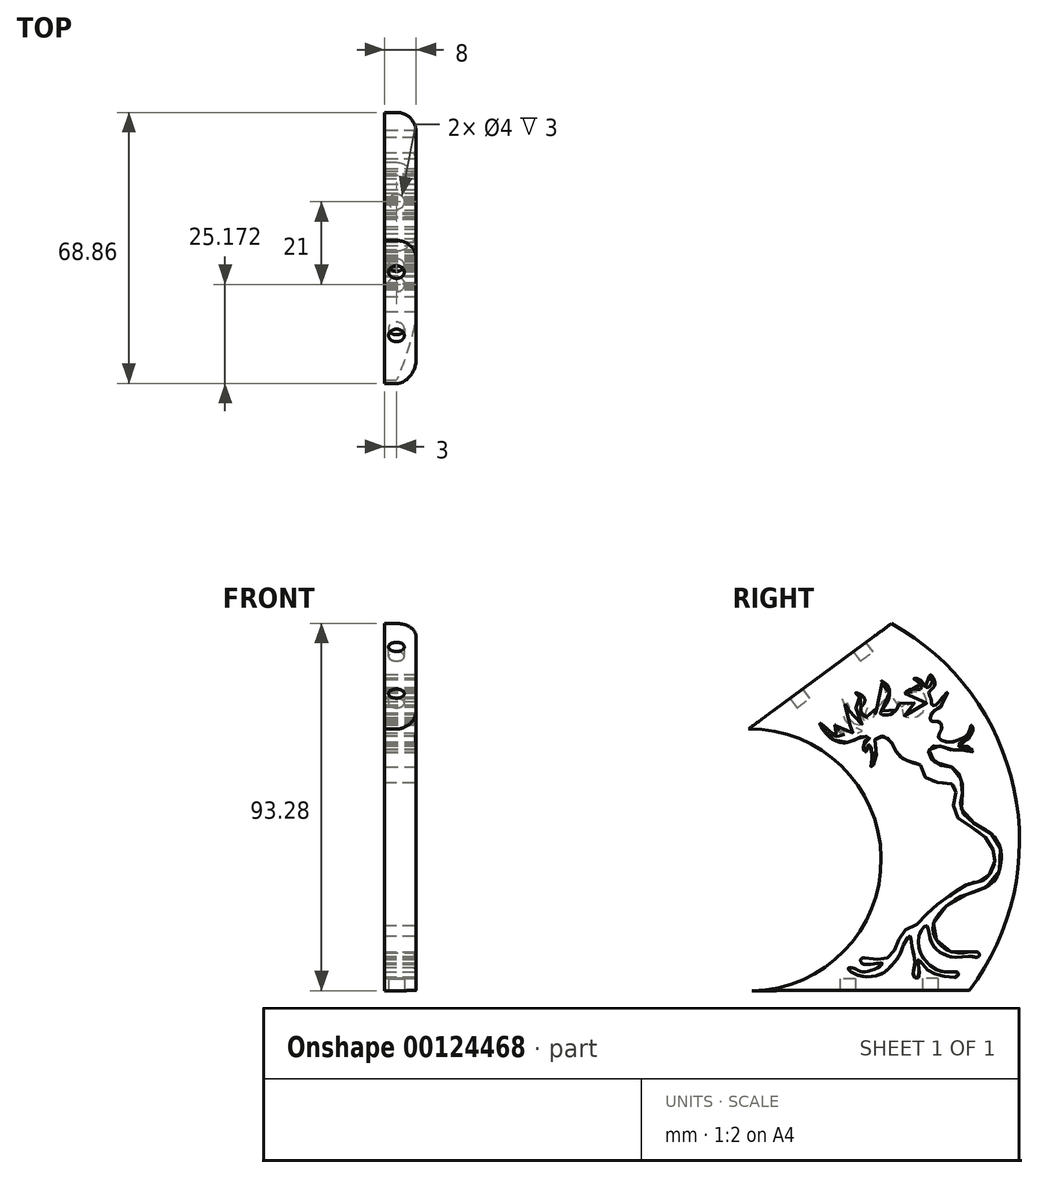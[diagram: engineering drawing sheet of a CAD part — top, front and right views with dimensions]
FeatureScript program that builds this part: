
annotation { "Feature Type Name" : "Feature", "Feature Type Description" : "" }
export const myFeature = defineFeature(function(context is Context, id is Id, definition is map)
    precondition{}
    {
        {
            var Q0;
            Q0=qCreatedBy(makeId("Right.planeOp"),FACE);
            var sketch = newSketch(context, id + "F0", { "sketchPlane" : qUnion([Q0])});
            skLineSegment(sketch, "E0", {"start": v(-38.95, 23.05) * mm, "end": v(-2.61, 49.85) * mm});
            skArc(sketch, "E1", {"start": v(-38.02, -43.43) * mm, "mid": v(-5.25, -9.73) * mm, "end": v(-38.95, 23.05) * mm});
            skArc(sketch, "E2", {"start": v(17.23, -43.32) * mm, "mid": v(28.53, 7.78) * mm, "end": v(-2.61, 49.85) * mm});
            skLineSegment(sketch, "E3", {"start": v(-38.02, -43.43) * mm, "end": v(17.23, -43.32) * mm});
            skArc(sketch, "E4.0", {"start": v(14.53, -41.3) * mm, "mid": v(25.24, 7.08) * mm, "end": v(-4.24, 46.9) * mm});
            skLineSegment(sketch, "E5", {"start": v(-4.24, 46.9) * mm, "end": v(-5.6, 47.65) * mm});
            skLineSegment(sketch, "E6", {"start": v(14.53, -41.3) * mm, "end": v(13, -43.33) * mm});
            skSolve(sketch);
        }
        {
            var Q0;
            Q0 = qSketchRegion(id + "F0", true);
            extrude(context, id + "F1", {"entities" : qUnion([Q0]), "oppositeDirection" : true, "depth" : 8 * mm});
        }
        {
            var Q0;
            Q0=makeQuery(id+"F1.opExtrude","CAP_FACE",FACE,{"disambiguationData":[OSD([sQuery(id+"F0.wireOp",EDGE,"E0"),sQuery(id+"F0.wireOp",EDGE,"E1"),sQuery(id+"F0.wireOp",EDGE,"E2"),sQuery(id+"F0.wireOp",EDGE,"E3")])],"isStart":true});
            var sketch = newSketch(context, id + "F2", { "sketchPlane" : qUnion([Q0])});
            skFitSpline(sketch, "E7", {"points": [v(4.67, 13.86) * mm, v(2.9, 14.45) * mm, v(-0.7, 16.28) * mm, v(-2.11, 18.67) * mm, v(-4.38, 21.18) * mm, v(-6.92, 20.26) * mm, v(-6.41, 17) * mm, v(-7.75, 13.26) * mm, v(-7.49, 17.25) * mm, v(-8.46, 19) * mm, v(-9.33, 17) * mm, v(-9.62, 19.7) * mm, v(-8.15, 20.8) * mm, v(-9.58, 21.26) * mm, v(-11.98, 20.2) * mm, v(-17.32, 20.28) * mm, v(-20.8, 24.44) * mm, v(-18.65, 22.73) * mm, v(-16.35, 21.16) * mm, v(-14.5, 21.7) * mm, v(-16.52, 22.58) * mm, v(-16.92, 24.07) * mm, v(-16.03, 22.88) * mm, v(-13.74, 22.44) * mm, v(-11.8, 21.99) * mm, v(-10.04, 22.46) * mm, v(-12.13, 23.55) * mm, v(-13.94, 24.64) * mm, v(-14.69, 26.12) * mm, v(-14.18, 28.48) * mm, v(-15.16, 30.73) * mm, v(-13.7, 29.56) * mm, v(-13.46, 28.36) * mm, v(-13.7, 26.36) * mm, v(-12.16, 24.47) * mm, v(-10.09, 24.24) * mm, v(-9.48, 25.75) * mm, v(-11.58, 26.98) * mm, v(-11.62, 28.54) * mm, v(-10.53, 30.64) * mm, v(-11.7, 32.24) * mm, v(-9.62, 31.09) * mm, v(-9.92, 29.08) * mm, v(-10.68, 28.21) * mm, v(-10.23, 27.01) * mm, v(-8.7, 28.47) * mm, v(-9.23, 27.1) * mm, v(-9.14, 26.26) * mm, v(-8.4, 25.5) * mm, v(-7.42, 25.87) * mm, v(-6.4, 27.9) * mm, v(-6.27, 28.46) * mm, v(-4.33, 30.58) * mm, v(-4.63, 33.99) * mm, v(-5.67, 35.46) * mm, v(-3.86, 34.43) * mm, v(-3.17, 32.53) * mm, v(-3.34, 30.6) * mm, v(-4.01, 29.23) * mm, v(-4.9, 28) * mm, v(-5.45, 26.99) * mm, v(-4.23, 26.6) * mm, v(-2.25, 27.14) * mm, v(-1.02, 29.1) * mm, v(-2.2, 31.06) * mm, v(-0.9, 30.16) * mm, v(-0.15, 28.69) * mm, v(1.46, 29.72) * mm, v(3.38, 29.77) * mm, v(1.97, 29.24) * mm, v(0.63, 28.56) * mm, v(0.17, 27.2) * mm, v(1.4, 25.95) * mm, v(4.8, 26.82) * mm, v(6.28, 30.56) * mm, v(4.23, 32.57) * mm, v(0.83, 32.13) * mm, v(2.44, 33.17) * mm, v(4.72, 33.08) * mm, v(4.61, 34.5) * mm, v(3.01, 35.89) * mm, v(4.88, 35.36) * mm, v(6.35, 33.55) * mm, v(7.46, 34.43) * mm, v(7.65, 35.36) * mm, v(7, 36.2) * mm, v(7.33, 36.78) * mm, v(8.14, 35.73) * mm, v(8.4, 34.24) * mm, v(7.5, 33.08) * mm, v(6.88, 32.14) * mm, v(7.42, 30.59) * mm, v(7.67, 29.17) * mm, v(8.6, 29.2) * mm, v(10.12, 30.8) * mm, v(11.58, 32.33) * mm, v(11.18, 31.18) * mm, v(10.43, 29.8) * mm, v(9.89, 28.72) * mm, v(8.76, 28.06) * mm, v(7.37, 26.6) * mm, v(7.49, 25.03) * mm, v(9.41, 24.94) * mm, v(10.1, 22.96) * mm, v(9.3, 20.95) * mm, v(11.68, 19.72) * mm, v(14.23, 20.22) * mm, v(16.96, 22) * mm, v(17.62, 24) * mm, v(18.07, 23.09) * mm, v(17.61, 21.58) * mm, v(16.16, 19.9) * mm, v(13.9, 19.07) * mm, v(14.9, 18.6) * mm, v(17.26, 18.51) * mm, v(18, 17.18) * mm, v(16.8, 17.43) * mm, v(15.07, 17.89) * mm, v(13, 17.7) * mm, v(10.79, 18.35) * mm, v(8.28, 18.86) * mm, v(6.95, 17.76) * mm, v(7.07, 15.98) * mm, v(10.33, 13.7) * mm, v(13.55, 13) * mm, v(15.13, 9.97) * mm, v(15.55, 7.42) * mm, v(14.9, 4.48) * mm, v(16.14, 0.88) * mm, v(20.85, -2.35) * mm, v(23.88, -4.74) * mm, v(25.24, -8.78) * mm, v(23.66, -15.24) * mm, v(19.31, -17.98) * mm, v(13.6, -20.26) * mm, v(8.6, -25.16) * mm, v(7.98, -28.8) * mm, v(10.27, -32.24) * mm, v(14.87, -33.9) * mm, v(19.5, -33.79) * mm, v(19.45, -34.86) * mm, v(17.8, -34.76) * mm, v(13.68, -34.93) * mm, v(11.25, -34.42) * mm, v(7.61, -31.45) * mm, v(6.3, -26.93) * mm, v(4.97, -28.03) * mm, v(4.2, -31.46) * mm, v(5.57, -35.28) * mm, v(10.47, -38.65) * mm, v(14.23, -38.82) * mm, v(13.96, -39.9) * mm, v(9.82, -39.5) * mm, v(6.57, -38.24) * mm, v(4.15, -35.38) * mm, v(4.36, -37.87) * mm, v(3.99, -40.3) * mm, v(2.9, -39.62) * mm, v(3.2, -37.47) * mm, v(3.06, -34.56) * mm, v(2.4, -31.01) * mm, v(2.01, -29.53) * mm, v(0.5, -31.63) * mm, v(-0.5, -34.36) * mm, v(-2.78, -37.26) * mm, v(-5.5, -39.4) * mm, v(-9.56, -39.88) * mm, v(-12.4, -38.97) * mm, v(-13.6, -37.74) * mm, v(-12.23, -37.74) * mm, v(-9.22, -38.68) * mm, v(-4.93, -36.6) * mm, v(-6.22, -36.5) * mm, v(-10.06, -36.52) * mm, v(-10.3, -35.32) * mm, v(-7.53, -35.25) * mm, v(-4.4, -35.38) * mm, v(-2.5, -34.12) * mm, v(-1.07, -31.45) * mm, v(0.35, -28.43) * mm, v(3.65, -26.78) * mm, v(7.2, -23.06) * mm, v(11.04, -20.18) * mm, v(17.2, -16.26) * mm, v(21.1, -15.1) * mm, v(23.56, -10.86) * mm, v(23.16, -7.74) * mm, v(20.23, -3.5) * mm, v(14.52, 0.2) * mm, v(13.13, 4.37) * mm, v(13.82, 7.94) * mm, v(11.44, 9.45) * mm, v(6.65, 9.97) * mm, v(4.67, 13.86) * mm]});
            skSolve(sketch);
        }
        {
            var Q0;
            Q0=makeQuery(id+"F1.opExtrude","CAP_EDGE",EDGE,{"disambiguationData":[OSD([sQuery(id+"F0.wireOp",EDGE,"E1")])],"isStart":true});
            var Q1;
            Q1=makeQuery(id+"F1.opExtrude","CAP_EDGE",EDGE,{"disambiguationData":[OSD([sQuery(id+"F0.wireOp",EDGE,"E2")])],"isStart":true});
            fillet(context, id + "F3", {"entities" : qUnion([Q0, Q1]), "radius" : 5 * mm, "tangentPropagation" : true, "allowEdgeOverflow" : false});
        }
        {
            var Q0;
            Q0 = qSketchRegion(id + "F2", true);
            extrude(context, id + "F4", {"entities" : qUnion([Q0]), "operationType" : NewBodyOperationType.REMOVE, "endBound" : BoundingType.SYMMETRIC, "oppositeDirection" : true, "depth" : 25 * mm});
        }
        {
            var Q0;
            Q0=makeQuery(id+"F1.opExtrude","SWEPT_FACE",FACE,{"disambiguationData":[OSD([sQuery(id+"F0.wireOp",EDGE,"E0")])]});
            var sketch = newSketch(context, id + "F5", { "sketchPlane" : qUnion([Q0])});
            skLineSegment(sketch, "E8", {"start": v(-5, -17.66) * mm, "end": v(-5, 21.51) * mm, "construction": true});
            skCircle(sketch, "E9", {"center": v(-5, 17.49) * mm, "radius": 2 * mm});
            skCircle(sketch, "E10", {"center": v(-5, -2.51) * mm, "radius": 2 * mm});
            skSolve(sketch);
        }
        {
            var Q0;
            Q0 = qSketchRegion(id + "F5", true);
            extrude(context, id + "F6", {"entities" : qUnion([Q0]), "operationType" : NewBodyOperationType.REMOVE, "oppositeDirection" : true, "depth" : 3 * mm});
        }
        {
            var Q0;
            Q0=makeQuery(id+"F1.opExtrude","SWEPT_FACE",FACE,{"disambiguationData":[OSD([sQuery(id+"F0.wireOp",EDGE,"E3")])]});
            var sketch = newSketch(context, id + "F7", { "sketchPlane" : qUnion([Q0])});
            skLineSegment(sketch, "E11", {"start": v(-5, -17.14) * mm, "end": v(-5, 28.46) * mm, "construction": true});
            skCircle(sketch, "E12", {"center": v(-5, -7.14) * mm, "radius": 2 * mm});
            skCircle(sketch, "E13", {"center": v(-5, 13.86) * mm, "radius": 2 * mm});
            skSolve(sketch);
        }
        {
            var Q0;
            Q0 = qSketchRegion(id + "F7", true);
            extrude(context, id + "F8", {"entities" : qUnion([Q0]), "operationType" : NewBodyOperationType.REMOVE, "oppositeDirection" : true, "depth" : 3 * mm});
        }
    });
